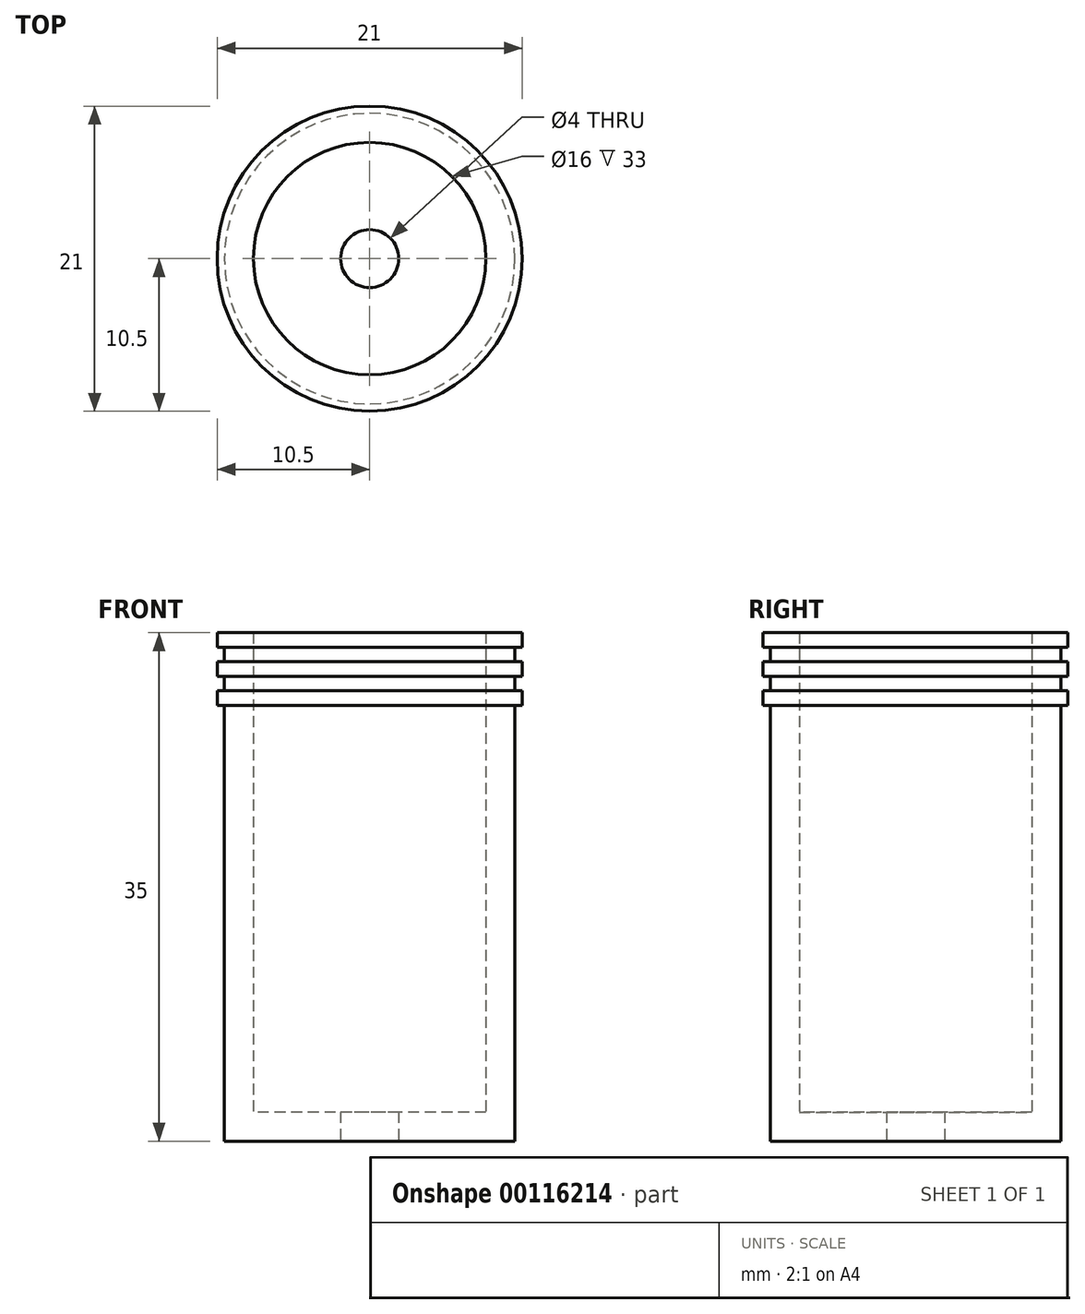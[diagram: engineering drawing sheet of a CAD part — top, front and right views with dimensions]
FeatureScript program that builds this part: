
annotation { "Feature Type Name" : "Feature", "Feature Type Description" : "" }
export const myFeature = defineFeature(function(context is Context, id is Id, definition is map)
    precondition{}
    {
        {
            var Q0;
            Q0=qCreatedBy(makeId("Top.planeOp"),FACE);
            var sketch = newSketch(context, id + "F0", { "sketchPlane" : qUnion([Q0])});
            skCircle(sketch, "E0", {"center": v(0, 0) * mm, "radius": 10 * mm});
            skCircle(sketch, "E1", {"center": v(0, 0) * mm, "radius": 2 * mm});
            skSolve(sketch);
        }
        {
            var Q0;
            Q0 = qSketchRegion(id + "F0", true);
            extrude(context, id + "F1", {"entities" : qUnion([Q0]), "depth" : 2 * mm});
        }
        {
            var Q0;
            Q0=makeQuery(id+"F1.opExtrude","CAP_FACE",FACE,{"disambiguationData":[OSD([sQuery(id+"F0.wireOp",EDGE,"E0"),sQuery(id+"F0.wireOp",EDGE,"E1")])],"isStart":false});
            var sketch = newSketch(context, id + "F2", { "sketchPlane" : qUnion([Q0])});
            skCircle(sketch, "E2", {"center": v(0, 0) * mm, "radius": 8 * mm});
            skSolve(sketch);
        }
        {
            var Q0;
            Q0=makeQuery(id+"F2.imprint","IMPRINT",FACE,{"disambiguationData":[TD([[makeQuery(id+"F2.imprint","IMPRINT",EDGE,{"derivedFrom":sQuery(id+"F2.wireOp",EDGE,"E2")}),-1.0]])]});
            extrude(context, id + "F3", {"entities" : qUnion([Q0]), "operationType" : NewBodyOperationType.ADD, "depth" : 28 * mm});
        }
        {
            var Q0;
            Q0=makeQuery(id+"F3.opExtrude","CAP_FACE",FACE,{"disambiguationData":[OSD([sQuery(id+"F0.wireOp",EDGE,"E0"),sQuery(id+"F2.wireOp",EDGE,"E2")])],"isStart":false});
            var sketch = newSketch(context, id + "F4", { "sketchPlane" : qUnion([Q0])});
            skCircle(sketch, "E3", {"center": v(0, 0) * mm, "radius": 8 * mm});
            skCircle(sketch, "E4", {"center": v(0, 0) * mm, "radius": 10.5 * mm});
            skSolve(sketch);
        }
        {
            var Q0;
            Q0 = qSketchRegion(id + "F4", true);
            extrude(context, id + "F5", {"entities" : qUnion([Q0]), "operationType" : NewBodyOperationType.ADD, "depth" : 1 * mm});
        }
        {
            var Q0;
            Q0=makeQuery(id+"F5.opExtrude","CAP_FACE",FACE,{"disambiguationData":[OSD([sQuery(id+"F4.wireOp",EDGE,"E3"),sQuery(id+"F4.wireOp",EDGE,"E4")])],"isStart":false});
            var sketch = newSketch(context, id + "F6", { "sketchPlane" : qUnion([Q0])});
            skCircle(sketch, "E5", {"center": v(0, 0) * mm, "radius": 10 * mm});
            skCircle(sketch, "E6", {"center": v(0, 0) * mm, "radius": 8 * mm});
            skSolve(sketch);
        }
        {
            var Q0;
            Q0 = qSketchRegion(id + "F6", true);
            extrude(context, id + "F7", {"entities" : qUnion([Q0]), "operationType" : NewBodyOperationType.ADD, "depth" : 1 * mm});
        }
        {
            var Q0;
            Q0=makeQuery(id+"F7.opExtrude","CAP_FACE",FACE,{"disambiguationData":[OSD([sQuery(id+"F6.wireOp",EDGE,"E5"),sQuery(id+"F6.wireOp",EDGE,"E6")])],"isStart":false});
            var sketch = newSketch(context, id + "F8", { "sketchPlane" : qUnion([Q0])});
            skCircle(sketch, "E7", {"center": v(0, 0) * mm, "radius": 8 * mm});
            skCircle(sketch, "E8", {"center": v(0, 0) * mm, "radius": 10.5 * mm});
            skSolve(sketch);
        }
        {
            var Q0;
            Q0 = qSketchRegion(id + "F8", true);
            extrude(context, id + "F9", {"entities" : qUnion([Q0]), "operationType" : NewBodyOperationType.ADD, "depth" : 1 * mm});
        }
        {
            var Q0;
            Q0=makeQuery(id+"F9.opExtrude","CAP_FACE",FACE,{"disambiguationData":[OSD([sQuery(id+"F8.wireOp",EDGE,"E7"),sQuery(id+"F8.wireOp",EDGE,"E8")])],"isStart":false});
            var sketch = newSketch(context, id + "F10", { "sketchPlane" : qUnion([Q0])});
            skCircle(sketch, "E9", {"center": v(0, 0) * mm, "radius": 10 * mm});
            skCircle(sketch, "E10", {"center": v(0, 0) * mm, "radius": 8 * mm});
            skSolve(sketch);
        }
        {
            var Q0;
            Q0 = qSketchRegion(id + "F10", true);
            extrude(context, id + "F11", {"entities" : qUnion([Q0]), "operationType" : NewBodyOperationType.ADD, "depth" : 1 * mm});
        }
        {
            var Q0;
            Q0=makeQuery(id+"F11.opExtrude","CAP_FACE",FACE,{"disambiguationData":[OSD([sQuery(id+"F10.wireOp",EDGE,"E9"),sQuery(id+"F10.wireOp",EDGE,"E10")])],"isStart":false});
            var sketch = newSketch(context, id + "F12", { "sketchPlane" : qUnion([Q0])});
            skCircle(sketch, "E11", {"center": v(0, 0) * mm, "radius": 8 * mm});
            skCircle(sketch, "E12", {"center": v(0, 0) * mm, "radius": 10.5 * mm});
            skSolve(sketch);
        }
        {
            var Q0;
            Q0 = qSketchRegion(id + "F12", true);
            extrude(context, id + "F13", {"entities" : qUnion([Q0]), "operationType" : NewBodyOperationType.ADD, "depth" : 1 * mm});
        }
    });
